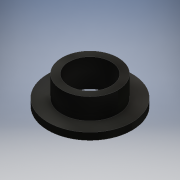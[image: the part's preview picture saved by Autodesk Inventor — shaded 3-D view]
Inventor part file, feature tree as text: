
AUTODESK INVENTOR PART (.ipt)
format: ipt  version: 2016 (Build 200138000, 138)  size: 108,032 bytes
history: native  units: mm
features: extrude x2, other x1, sketch x1
ambient origin geometry x8: Origin, YZ Plane, XZ Plane, XY Plane, X Axis, Y Axis, Z Axis, Center Point
bodies: Body1 (feature_tree)
feature tree (4):
  other  "ソリッド1"
  sketch  "スケッチ1"
  extrude  "押し出し1"  Depth=6.0mm
  extrude  "押し出し2"  Depth=8.0mm
